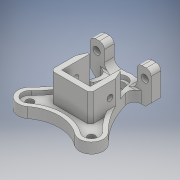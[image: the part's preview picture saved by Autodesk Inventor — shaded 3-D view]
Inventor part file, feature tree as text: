
AUTODESK INVENTOR PART (.ipt)
format: ipt  version: 2018 (Build 220112000, 112)  size: 389,632 bytes
history: native  units: mm
features: extrude x11, sketch x11, fillet x5, projected_geometry x5, chamfer x3, plane x1, mirror x1
ambient origin geometry x8: Origin, YZ Plane, XZ Plane, XY Plane, X Axis, Y Axis, Z Axis, Center Point
bodies: Solid1 (feature_tree)
feature tree (37):
  extrude  "Extrusion1"  Depth=42.0mm
  extrude  "Extrusion2"  Depth=21.0mm
  extrude  "Extrusion3"  Depth=28.0mm
  chamfer  "Chamfer1"  Distance=4.5mm
  extrude  "Extrusion4"  Depth=10.0mm TaperAngle=0.0deg
  extrude  "Extrusion5"  Depth=4.0mm
  extrude  "Extrusion6"  Depth=4.0mm
  chamfer  "Chamfer2"  Distance=20.0mm
  plane  "Work Plane1"
  extrude  "Extrusion8"  Depth=3.0mm
  extrude  "Extrusion7"  Depth=3.0mm TaperAngle=0.0deg
  fillet  "Fillet1"  Radius=4.2mm
  extrude  "Extrusion12"  Depth=10.0mm
  extrude  "Extrusion13"  Depth=10.0mm
  fillet  "Fillet3"  Radius=15.0mm
  extrude  "Extrusion14"  Depth=1.0mm TaperAngle=0.0deg
  fillet  "Fillet4"  Radius=1.0mm
  chamfer  "Chamfer4"  Distance=5.15mm
  mirror  "Mirror2"
  fillet  "Fillet5"  Radius=3.0mm
  fillet  "Fillet6"  Radius=19.0mm
  sketch  "Sketch1"  dims[d0=17.0mm d1=42.0mm]
  sketch  "Sketch2"  dims[d2=22.0mm d3=21.0mm]
  sketch  "Sketch3"  dims[d4=68.0mm d5=28.0mm d6=4.5mm d7=0.0mm]
  sketch  "Sketch4"  dims[d8=7.3mm d9=10.0mm d10=0.0mm]
  projected_geometry  "Projected Loop1"
  projected_geometry  "Projected Loop2"
  sketch  "Sketch5"  dims[d11=20.5mm d12=4.0mm]
  sketch  "Sketch6"  dims[d13=4.0mm d14=4.0mm]
  sketch  "Sketch9"  dims[d15=20.0mm d16=20.0mm d17=0.0mm]
  projected_geometry  "Projected Loop5"
  sketch  "Sketch16"  dims[d18=2.0mm d19=2.0mm d20=45.0deg d21=3.0mm]
  projected_geometry  "Projected Loop10"
  sketch  "Sketch25"  dims[d23=3.0mm d25=3.0mm d26=0.0mm d27=4.2mm]
  sketch  "Sketch26"  dims[d28=20.0mm d29=0.0mm d30=10.0mm]
  projected_geometry  "Projected Loop16"
  sketch  "Sketch27"  dims[d31=10.0mm d32=10.0mm d33=15.0mm d34=20.0mm d35=0.0mm d36=1.0mm d37=2.0mm d38=45.0deg d39=5.15mm d40=3.0mm d44=19.0mm d45=3.0mm d46=5.2mm d47=17.0mm d48=10.0mm d49=14.0mm d50=7.0mm d51=0.0mm d54=1.0mm d55=0.0mm d62=3.5mm d71=1.0mm d72=0.0mm d73=1.0mm d74=0.0mm d75=5.0mm d76=1.0mm d77=0.0mm d78=5.0mm d79=4.0mm d80=2.0mm d81=45.0deg d82=5.0mm d83=1.0mm]
